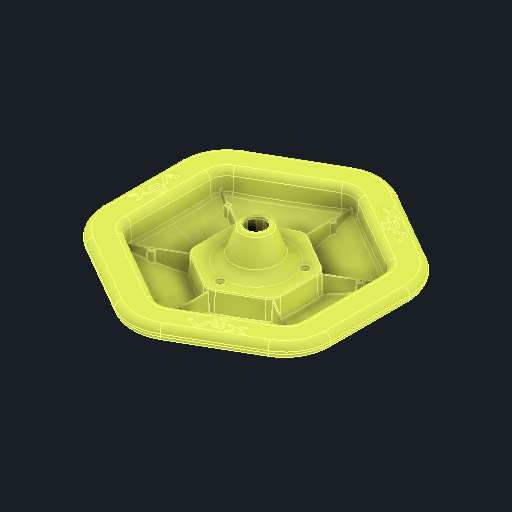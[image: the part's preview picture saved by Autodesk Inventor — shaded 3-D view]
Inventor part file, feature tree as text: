
AUTODESK INVENTOR PART (.ipt)
format: ipt  version: 2025 (Build 290162000, 162)  size: 4,256,768 bytes
history: native  units: in
note: dims shown in document units (in); Inventor stores cm internally (conversion verified against a paired STEP export)
features: fillet x1
ambient origin geometry x8: Origin, YZ Plane, XZ Plane, XY Plane, X Axis, Y Axis, Z Axis, Center Point
bodies: Solid1 (feature_tree)
feature tree (1):
  fillet  "Fillet265"  [1 undecoded]
note: 1 required parameter value undecoded (feature->parameter linkage not recoverable at this tier; creation-order binding heuristic only, values carry confidence <= 0.55)
